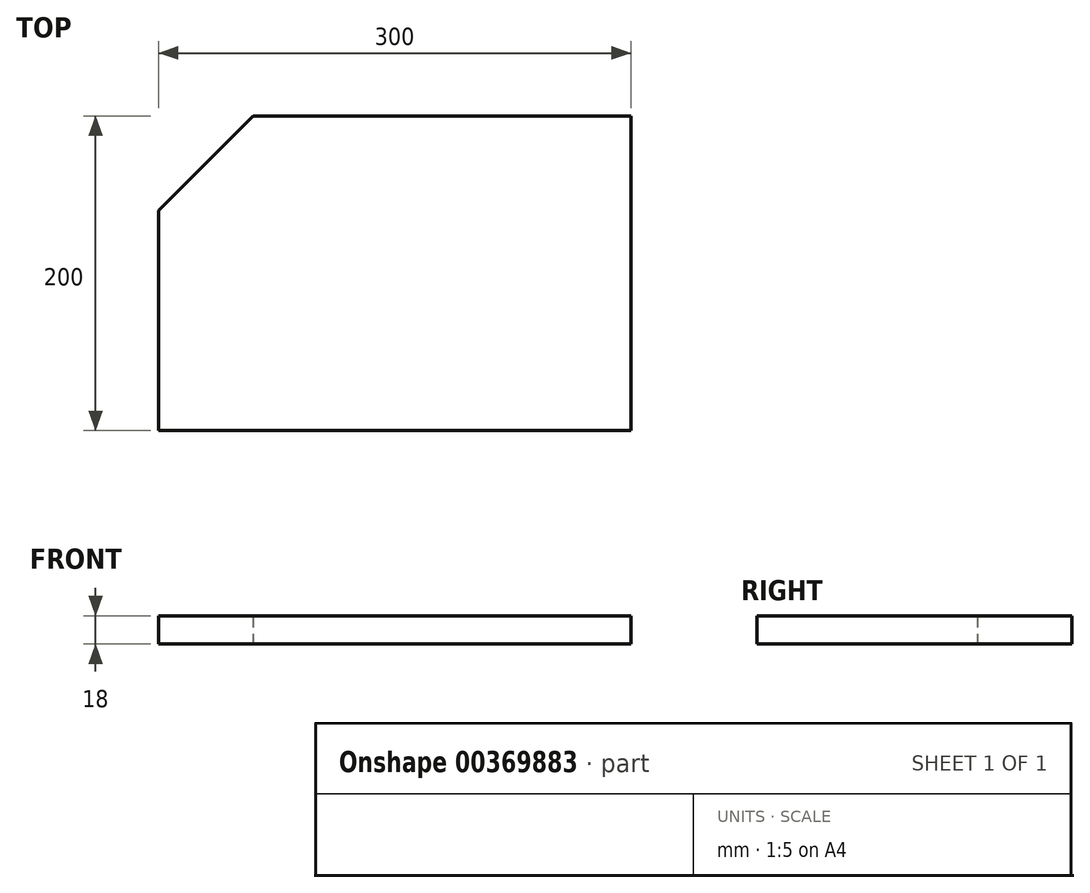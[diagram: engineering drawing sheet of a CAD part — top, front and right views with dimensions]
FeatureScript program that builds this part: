
annotation { "Feature Type Name" : "Feature", "Feature Type Description" : "" }
export const myFeature = defineFeature(function(context is Context, id is Id, definition is map)
    precondition{}
    {
        {
            var Q0;
            Q0=qCreatedBy(makeId("Top.planeOp"),FACE);
            var sketch = newSketch(context, id + "F0", { "sketchPlane" : qUnion([Q0])});
            skLineSegment(sketch, "E0.bottom", {"start": v(0, 0) * mm, "end": v(300, 0) * mm});
            skLineSegment(sketch, "E0.top", {"start": v(60, 200) * mm, "end": v(300, 200) * mm});
            skLineSegment(sketch, "E0.left", {"start": v(0, 0) * mm, "end": v(0, 140) * mm});
            skLineSegment(sketch, "E0.right", {"start": v(300, 0) * mm, "end": v(300, 200) * mm});
            skLineSegment(sketch, "E1", {"start": v(0, 140) * mm, "end": v(60, 200) * mm});
            skSolve(sketch);
        }
        {
            var Q0;
            Q0=makeQuery(id+"F0.imprint","IMPRINT",FACE,{"disambiguationData":[TD([[makeQuery(id+"F0.imprint","IMPRINT",EDGE,{"derivedFrom":sQuery(id+"F0.wireOp",EDGE,"E0.bottom")}),1.0]])]});
            extrude(context, id + "F1", {"entities" : qUnion([Q0]), "depth" : 18 * mm});
        }
    });
